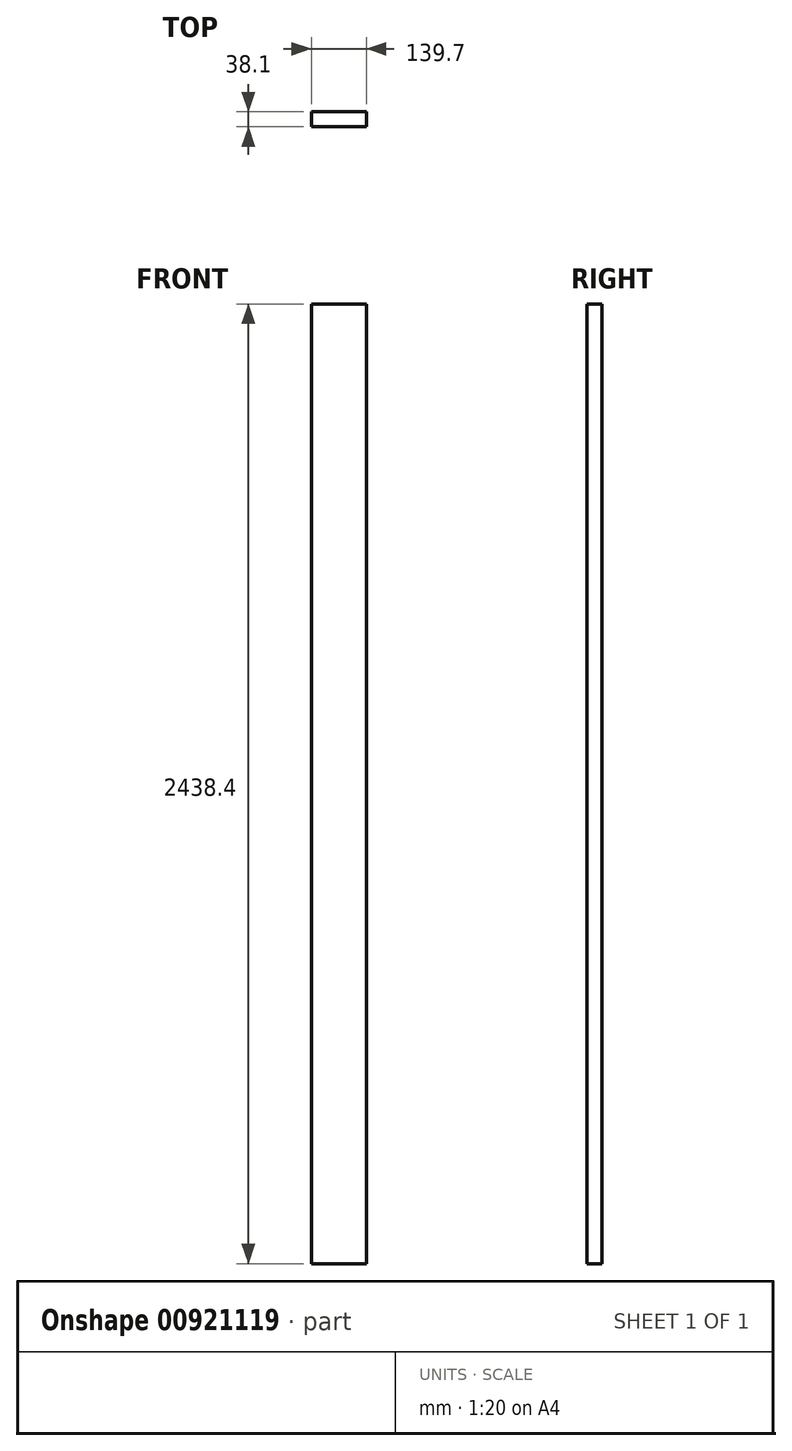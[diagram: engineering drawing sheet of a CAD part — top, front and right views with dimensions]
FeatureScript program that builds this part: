
annotation { "Feature Type Name" : "Feature", "Feature Type Description" : "" }
export const myFeature = defineFeature(function(context is Context, id is Id, definition is map)
    precondition{}
    {
        {
            var Q0;
            Q0=qCreatedBy(makeId("Top.planeOp"),FACE);
            var sketch = newSketch(context, id + "F0", { "sketchPlane" : qUnion([Q0])});
            skLineSegment(sketch, "E0.bottom", {"start": v(0, 0) * mm, "end": v(139.7, 0) * mm});
            skLineSegment(sketch, "E0.top", {"start": v(0, -38.1) * mm, "end": v(139.7, -38.1) * mm});
            skLineSegment(sketch, "E0.left", {"start": v(0, 0) * mm, "end": v(0, -38.1) * mm});
            skLineSegment(sketch, "E0.right", {"start": v(139.7, 0) * mm, "end": v(139.7, -38.1) * mm});
            skSolve(sketch);
        }
        {
            var Q0;
            Q0=makeQuery(id+"F0.imprint","IMPRINT",FACE,{"disambiguationData":[TD([[makeQuery(id+"F0.imprint","IMPRINT",EDGE,{"derivedFrom":sQuery(id+"F0.wireOp",EDGE,"E0.bottom")}),-1.0]])]});
            extrude(context, id + "F1", {"entities" : qUnion([Q0]), "depth" : 2438.4 * mm, "offsetDistance" : 25.4 * mm});
        }
    });
